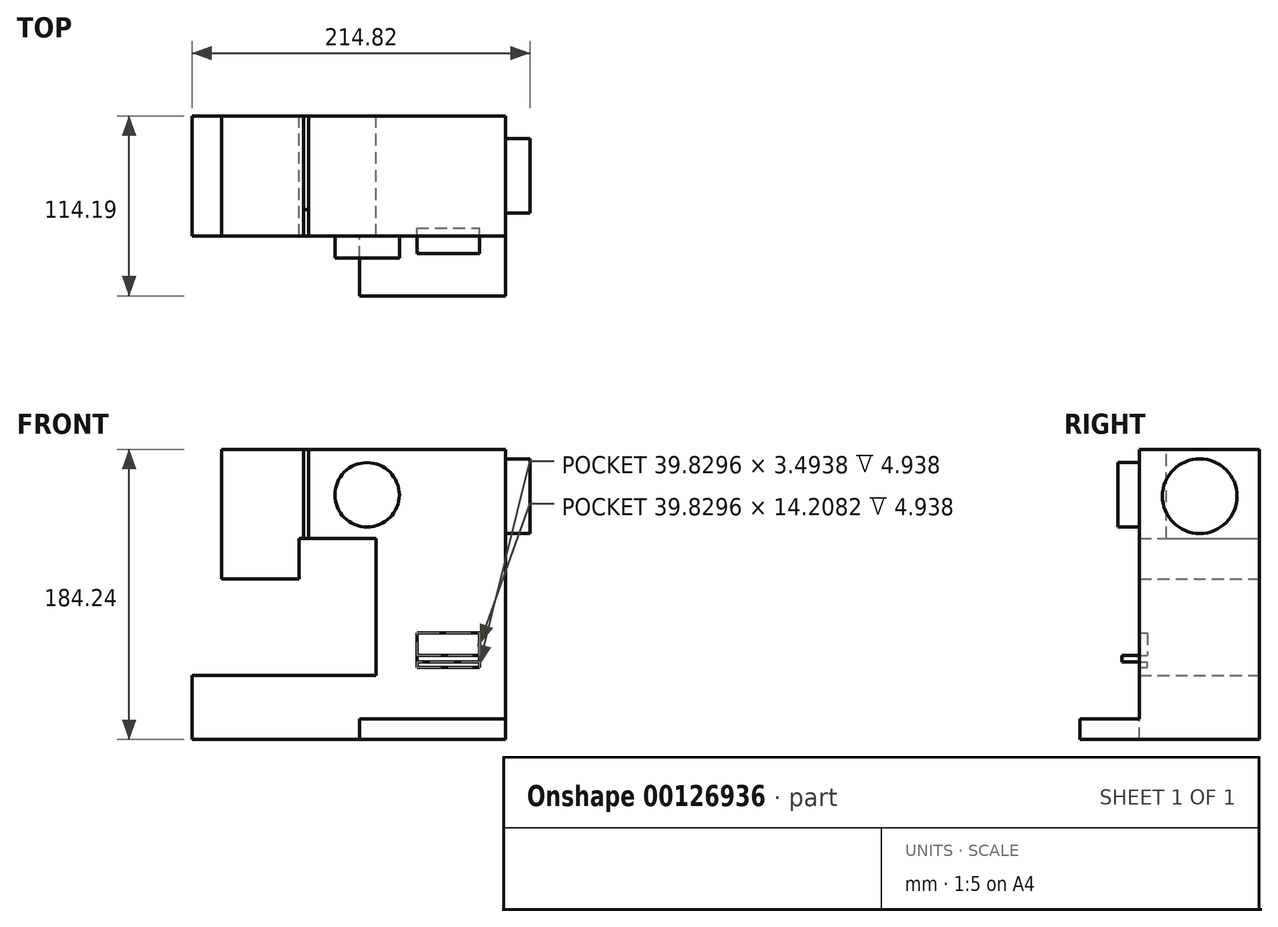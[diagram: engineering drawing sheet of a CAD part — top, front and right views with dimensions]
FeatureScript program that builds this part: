
annotation { "Feature Type Name" : "Feature", "Feature Type Description" : "" }
export const myFeature = defineFeature(function(context is Context, id is Id, definition is map)
    precondition{}
    {
        {
            var Q0;
            Q0=qCreatedBy(makeId("Front.planeOp"),FACE);
            var sketch = newSketch(context, id + "F0", { "sketchPlane" : qUnion([Q0])});
            skLineSegment(sketch, "E0", {"start": v(-73.25, 5.39) * mm, "end": v(-23.9, 5.39) * mm});
            skLineSegment(sketch, "E1", {"start": v(-23.9, 5.39) * mm, "end": v(-23.9, 31.04) * mm});
            skLineSegment(sketch, "E2", {"start": v(-23.9, 31.04) * mm, "end": v(24.87, 31.04) * mm});
            skLineSegment(sketch, "E3", {"start": v(24.87, 31.04) * mm, "end": v(24.87, -56.11) * mm});
            skLineSegment(sketch, "E4", {"start": v(24.87, -56.11) * mm, "end": v(-92.06, -56.11) * mm});
            skLineSegment(sketch, "E5", {"start": v(-92.06, -56.11) * mm, "end": v(-92.06, -96.65) * mm});
            skLineSegment(sketch, "E6", {"start": v(-92.06, -96.65) * mm, "end": v(14.51, -96.65) * mm});
            skLineSegment(sketch, "E7", {"start": v(14.51, -96.65) * mm, "end": v(14.51, -83.6) * mm});
            skLineSegment(sketch, "E8", {"start": v(14.51, -83.6) * mm, "end": v(107.21, -83.6) * mm});
            skLineSegment(sketch, "E9", {"start": v(107.21, -83.6) * mm, "end": v(107.21, -96.65) * mm});
            skLineSegment(sketch, "E10", {"start": v(107.21, -96.65) * mm, "end": v(14.51, -96.65) * mm});
            skLineSegment(sketch, "E11", {"start": v(107.21, -83.6) * mm, "end": v(107.21, 87.59) * mm});
            skLineSegment(sketch, "E12", {"start": v(107.21, 87.59) * mm, "end": v(-73.25, 87.59) * mm});
            skLineSegment(sketch, "E13", {"start": v(-73.25, 87.59) * mm, "end": v(-73.25, 5.39) * mm});
            skCircle(sketch, "E14", {"center": v(19.17, 58.7) * mm, "radius": 20.47 * mm});
            skLineSegment(sketch, "E15", {"start": v(50.85, -51) * mm, "end": v(90.68, -51) * mm});
            skLineSegment(sketch, "E16", {"start": v(90.68, -51) * mm, "end": v(90.68, -29.1) * mm});
            skLineSegment(sketch, "E17", {"start": v(50.85, -43.31) * mm, "end": v(90.68, -43.31) * mm});
            skLineSegment(sketch, "E18", {"start": v(90.68, -43.31) * mm, "end": v(90.68, -47.5) * mm});
            skLineSegment(sketch, "E19", {"start": v(90.68, -47.5) * mm, "end": v(50.85, -47.5) * mm});
            skLineSegment(sketch, "E20", {"start": v(50.85, -47.5) * mm, "end": v(50.85, -43.31) * mm});
            skLineSegment(sketch, "E21", {"start": v(90.68, -29.1) * mm, "end": v(50.85, -29.1) * mm});
            skLineSegment(sketch, "E22", {"start": v(50.85, -29.1) * mm, "end": v(50.85, -51) * mm});
            skLineSegment(sketch, "E23", {"start": v(-21.11, 87.59) * mm, "end": v(-21.11, 31.04) * mm});
            skLineSegment(sketch, "E24", {"start": v(-21.11, 31.04) * mm, "end": v(-18.03, 31.04) * mm});
            skLineSegment(sketch, "E25", {"start": v(-18.03, 31.04) * mm, "end": v(-18.03, 87.59) * mm});
            skLineSegment(sketch, "E26", {"start": v(-18.03, 87.59) * mm, "end": v(-21.11, 87.59) * mm});
            skSolve(sketch);
        }
        {
            var Q0;
            Q0=qCreatedBy(makeId("Right.planeOp"),FACE);
            var sketch = newSketch(context, id + "F1", { "sketchPlane" : qUnion([Q0])});
            skCircle(sketch, "E27", {"center": v(-37.94, 57.86) * mm, "radius": 23.72 * mm});
            skSolve(sketch);
        }
        {
            var Q0;
            Q0=makeQuery(id+"F0.imprint","IMPRINT",FACE,{"disambiguationData":[TD([[makeQuery(id+"F0.imprint","IMPRINT",EDGE,{"derivedFrom":sQuery(id+"F0.wireOp",EDGE,"E0")}),1.0]])]});
            var Q1;
            {var subQ0=sQuery(id+"F0.wireOp",EDGE,"E3");Q1=makeQuery(id+"F0.imprint","IMPRINT",FACE,{"disambiguationData":[TD([[makeQuery(id+"F0.imprint","IMPRINT",EDGE,{"derivedFrom":subQ0}),1.0]])]});}
            extrude(context, id + "F2", {"entities" : qUnion([Q0, Q1]), "depth" : 76.2 * mm});
        }
        {
            var Q0;
            Q0=makeQuery(id+"F0.imprint","IMPRINT",FACE,{"disambiguationData":[TD([[makeQuery(id+"F0.imprint","IMPRINT",EDGE,{"derivedFrom":sQuery(id+"F0.wireOp",EDGE,"E14")}),1.0]])]});
            extrude(context, id + "F3", {"entities" : qUnion([Q0]), "operationType" : NewBodyOperationType.ADD, "depth" : 90.03 * mm});
        }
        {
            var Q0;
            {var subQ2=sQuery(id+"F0.wireOp",EDGE,"E17");Q0=makeQuery(id+"F0.imprint","IMPRINT",FACE,{"disambiguationData":[TD([[makeQuery(id+"F0.imprint","IMPRINT",EDGE,{"derivedFrom":subQ2}),1.0]])]});}
            var Q1;
            {var subQ0=sQuery(id+"F0.wireOp",EDGE,"E15");Q1=makeQuery(id+"F0.imprint","IMPRINT",FACE,{"disambiguationData":[TD([[makeQuery(id+"F0.imprint","IMPRINT",EDGE,{"derivedFrom":subQ0}),1.0]])]});}
            extrude(context, id + "F4", {"entities" : qUnion([Q0, Q1]), "operationType" : NewBodyOperationType.ADD, "depth" : 71.26 * mm});
        }
        {
            var Q0;
            {var subQ0=sQuery(id+"F0.wireOp",EDGE,"E17");Q0=makeQuery(id+"F0.imprint","IMPRINT",FACE,{"disambiguationData":[TD([[makeQuery(id+"F0.imprint","IMPRINT",EDGE,{"derivedFrom":subQ0}),-1.0]])]});}
            extrude(context, id + "F5", {"entities" : qUnion([Q0]), "operationType" : NewBodyOperationType.ADD, "depth" : 87.28 * mm});
        }
        {
            var Q0;
            Q0=makeQuery(id+"F0.imprint","IMPRINT",FACE,{"disambiguationData":[TD([[makeQuery(id+"F0.imprint","IMPRINT",EDGE,{"derivedFrom":sQuery(id+"F0.wireOp",EDGE,"E7")}),-1.0]])]});
            extrude(context, id + "F6", {"entities" : qUnion([Q0]), "operationType" : NewBodyOperationType.ADD, "depth" : 114.19 * mm});
        }
        {
            var Q0;
            Q0=makeQuery(id+"F0.imprint","IMPRINT",FACE,{"disambiguationData":[TD([[makeQuery(id+"F0.imprint","IMPRINT",EDGE,{"derivedFrom":sQuery(id+"F0.wireOp",EDGE,"E23")}),1.0]])]});
            extrude(context, id + "F7", {"entities" : qUnion([Q0]), "depth" : 59.22 * mm});
        }
        {
            var Q0;
            Q0 = qSketchRegion(id + "F1", true);
            extrude(context, id + "F8", {"entities" : qUnion([Q0]), "operationType" : NewBodyOperationType.ADD, "depth" : 122.76 * mm});
        }
    });
